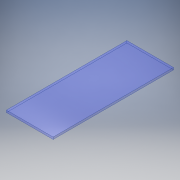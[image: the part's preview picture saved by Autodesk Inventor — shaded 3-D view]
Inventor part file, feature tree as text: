
AUTODESK INVENTOR PART (.ipt)
format: ipt  version: 2018.1 (Build 221171000, 171)  size: 113,152 bytes
history: native  units: mm
features: other x5, reference x4, extrude x2, sketch x2
ambient origin geometry x8: Origin, YZ Plane, XZ Plane, XY Plane, X Axis, Y Axis, Z Axis, Center Point
bodies: Solid1 (feature_tree)
feature tree (13):
  parser-record x2  (decoder bookkeeping rows leaked as tree rows — omitted from the tree; the rows remain in map.json)
  extrude  "Extrusion1"  Depth=284.0mm
  extrude  "Extrusion2"  TaperAngle=0.0deg  [1 undecoded]
  sketch  "Sketch1"  dims[d0=110.0mm d1=284.0mm]
  sketch  "Sketch2"  dims[d2=5.0mm d3=0.0mm d4=5.0mm d5=0.0mm]
  reference  "Reference1"
  reference  "Reference2"
  reference  "Reference3"
  reference  "Reference4"
  other  "tank_lid_assembly.iam"
  other  "tank_lid_handle_assembly:1"
  other  "tank_lid_handle_support:1"
note: 1 required parameter value undecoded (feature->parameter linkage not recoverable at this tier; creation-order binding heuristic only, values carry confidence <= 0.55)
note: 2 file-system paths scrubbed to <path> (originals preserved in map.json)
